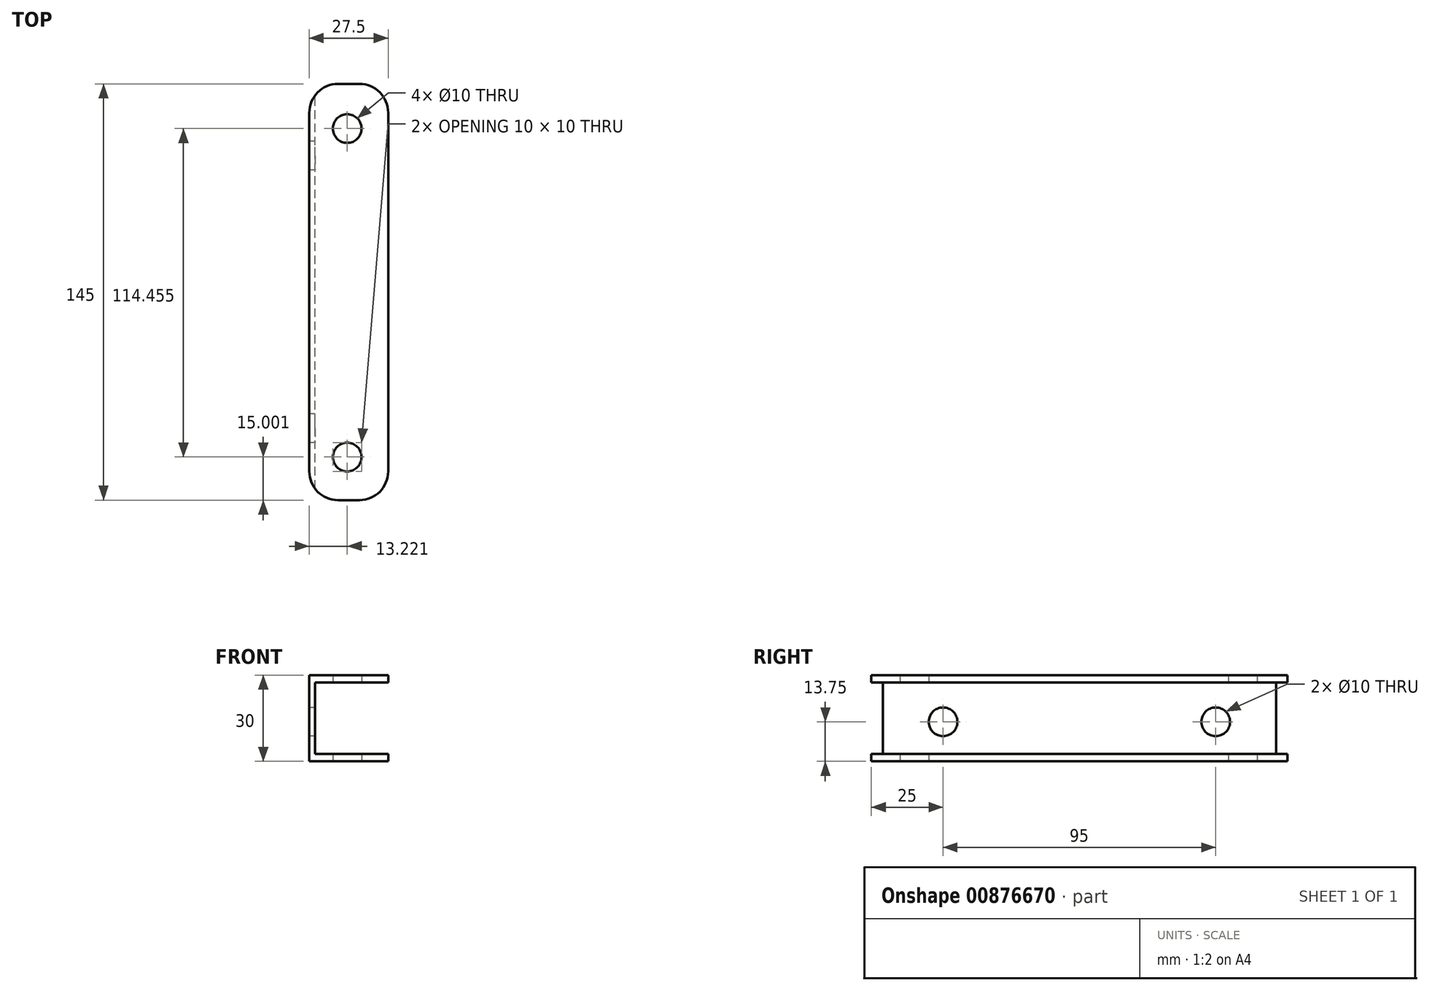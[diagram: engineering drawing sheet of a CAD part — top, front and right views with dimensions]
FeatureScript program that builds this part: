
annotation { "Feature Type Name" : "Feature", "Feature Type Description" : "" }
export const myFeature = defineFeature(function(context is Context, id is Id, definition is map)
    precondition{}
    {
        {
            var Q0;
            Q0=qCreatedBy(makeId("Front.planeOp"),FACE);
            var sketch = newSketch(context, id + "F0", { "sketchPlane" : qUnion([Q0])});
            skLineSegment(sketch, "E0.bottom", {"start": v(-74.99, 0) * mm, "end": v(-47.49, 0) * mm});
            skLineSegment(sketch, "E0.top", {"start": v(-74.99, 30) * mm, "end": v(-47.49, 30) * mm});
            skLineSegment(sketch, "E0.left", {"start": v(-74.99, 0) * mm, "end": v(-74.99, 30) * mm});
            skLineSegment(sketch, "E0.right", {"start": v(-47.49, 0) * mm, "end": v(-47.49, 2.5) * mm});
            skLineSegment(sketch, "E1.top", {"start": v(-47.49, 2.5) * mm, "end": v(-72.99, 2.5) * mm});
            skLineSegment(sketch, "E2.top", {"start": v(-47.49, 27.5) * mm, "end": v(-72.99, 27.5) * mm});
            skLineSegment(sketch, "E3.trimOffspring", {"start": v(-47.49, 27.5) * mm, "end": v(-47.49, 30) * mm});
            skPoint(sketch, "E2.left.start.orphan", {"position": v(-47.49, 15) * mm});
            skLineSegment(sketch, "E4", {"start": v(-72.99, 27.5) * mm, "end": v(-72.99, 2.5) * mm});
            skSolve(sketch);
        }
        {
            var Q0;
            Q0=qCreatedBy(makeId("Top.planeOp"),FACE);
            var sketch = newSketch(context, id + "F1", { "sketchPlane" : qUnion([Q0])});
            skLineSegment(sketch, "E5.bottom", {"start": v(-59.99, -290) * mm, "end": v(-54.99, -290) * mm});
            skCircle(sketch, "E6", {"center": v(-61.77, -15.54) * mm, "radius": 5 * mm});
            skCircle(sketch, "E7", {"center": v(-54.99, -290) * mm, "radius": 5 * mm});
            skCircle(sketch, "E8", {"center": v(-54.99, -260) * mm, "radius": 5 * mm});
            skCircle(sketch, "E9", {"center": v(-61.77, -130) * mm, "radius": 5 * mm});
            skLineSegment(sketch, "E10", {"start": v(-61.77, -15.54) * mm, "end": v(-61.77, -83.7) * mm});
            skSolve(sketch);
        }
        {
            var Q0;
            Q0=makeQuery(id+"F0.imprint","IMPRINT",FACE,{"disambiguationData":[TD([[makeQuery(id+"F0.imprint","IMPRINT",EDGE,{"derivedFrom":sQuery(id+"F0.wireOp",EDGE,"E0.bottom")}),1.0]])]});
            extrude(context, id + "F2", {"entities" : qUnion([Q0]), "depth" : 145 * mm, "offsetDistance" : 25 * mm});
        }
        {
            var Q0;
            Q0=makeQuery(id+"F1.imprint","IMPRINT",FACE,{"disambiguationData":[TD([[makeQuery(id+"F1.imprint","IMPRINT",EDGE,{"derivedFrom":sQuery(id+"F1.wireOp",EDGE,"E7")}),1.0]])]});
            var Q1;
            Q1=makeQuery(id+"F1.imprint","IMPRINT",FACE,{"disambiguationData":[TD([[makeQuery(id+"F1.imprint","IMPRINT",EDGE,{"derivedFrom":sQuery(id+"F1.wireOp",EDGE,"E8")}),1.0]])]});
            var Q2;
            Q2=makeQuery(id+"F1.imprint","IMPRINT",FACE,{"disambiguationData":[TD([[makeQuery(id+"F1.imprint","IMPRINT",EDGE,{"derivedFrom":sQuery(id+"F1.wireOp",EDGE,"E9")}),1.0]])]});
            var Q3;
            Q3=makeQuery(id+"F1.imprint","IMPRINT",FACE,{"disambiguationData":[TD([[makeQuery(id+"F1.imprint","IMPRINT",EDGE,{"derivedFrom":sQuery(id+"F1.wireOp",EDGE,"E6")}),1.0]])]});
            extrude(context, id + "F3", {"entities" : qUnion([Q0, Q1, Q2, Q3]), "operationType" : NewBodyOperationType.REMOVE, "depth" : 46 * mm, "offsetDistance" : 25 * mm});
        }
        {
            var Q0;
            Q0=makeQuery(id+"F2.opExtrude","CAP_EDGE",EDGE,{"disambiguationData":[OSD([sQuery(id+"F0.wireOp",EDGE,"E0.right")])],"isStart":true});
            var Q1;
            Q1=makeQuery(id+"F2.opExtrude","CAP_EDGE",EDGE,{"disambiguationData":[OSD([sQuery(id+"F0.wireOp",EDGE,"E3.trimOffspring")])],"isStart":true});
            var Q2;
            Q2=makeQuery(id+"F2.opExtrude","CAP_EDGE",EDGE,{"disambiguationData":[OSD([sQuery(id+"F0.wireOp",EDGE,"E3.trimOffspring")])],"isStart":false});
            var Q3;
            Q3=makeQuery(id+"F2.opExtrude","CAP_EDGE",EDGE,{"disambiguationData":[OSD([sQuery(id+"F0.wireOp",EDGE,"E0.right")])],"isStart":false});
            var Q4;
            Q4=makeQuery(id+"F2.opExtrude","CAP_EDGE",EDGE,{"disambiguationData":[OSD([sQuery(id+"F0.wireOp",EDGE,"E0.left")])],"isStart":true});
            var Q5;
            Q5=makeQuery(id+"F2.opExtrude","CAP_EDGE",EDGE,{"disambiguationData":[OSD([sQuery(id+"F0.wireOp",EDGE,"E0.left")])],"isStart":false});
            fillet(context, id + "F4", {"entities" : qUnion([Q0, Q1, Q2, Q3, Q4, Q5]), "radius" : 10 * mm, "tangentPropagation" : true, "allowEdgeOverflow" : false});
        }
        {
            var Q0;
            Q0=makeQuery(id+"F2.opExtrude","SWEPT_FACE",FACE,{"disambiguationData":[OSD([sQuery(id+"F0.wireOp",EDGE,"E0.left")])]});
            cPlane(context, id + "F5", {"entities" : qUnion([Q0]), "cplaneType" : CPlaneType.OFFSET, "offset" : 0 * mm, "width" : 150 * mm, "height" : 150 * mm});
        }
        {
            var Q0;
            Q0=qCreatedBy(id+"F5.planeOp",FACE);
            var sketch = newSketch(context, id + "F6", { "sketchPlane" : qUnion([Q0])});
            skLineSegment(sketch, "E11.bottom", {"start": v(10, 30) * mm, "end": v(130, 30) * mm});
            skLineSegment(sketch, "E11.top", {"start": v(10, 0) * mm, "end": v(130, 0) * mm});
            skLineSegment(sketch, "E11.left", {"start": v(10, 30) * mm, "end": v(10, 0) * mm});
            skLineSegment(sketch, "E11.right", {"start": v(130, 30) * mm, "end": v(130, 0) * mm});
            skLineSegment(sketch, "E12.bottom", {"start": v(130, 0) * mm, "end": v(25, 0) * mm});
            skLineSegment(sketch, "E12.top", {"start": v(130, 13.75) * mm, "end": v(25, 13.75) * mm});
            skLineSegment(sketch, "E12.left", {"start": v(130, 0) * mm, "end": v(130, 13.75) * mm});
            skLineSegment(sketch, "E12.right", {"start": v(25, 0) * mm, "end": v(25, 13.75) * mm});
            skLineSegment(sketch, "E13", {"start": v(120, 13.75) * mm, "end": v(130, 13.75) * mm});
            skCircle(sketch, "E14", {"center": v(25, 13.75) * mm, "radius": 5 * mm});
            skCircle(sketch, "E15", {"center": v(120, 13.75) * mm, "radius": 5 * mm});
            skSolve(sketch);
        }
        {
            var Q0;
            {var subQ0=sQuery(id+"F6.wireOp",EDGE,"E12.right");var subQ1=sQuery(id+"F6.wireOp",EDGE,"E12.top");var subQ2=makeQuery(id+"F6.imprint","INTERSECT",VERTEX,{"derivedFrom":[subQ1,subQ0]});Q0=makeQuery(id+"F6.imprint","IMPRINT",FACE,{"disambiguationData":[TD([[makeQuery(id+"F6.imprint","IMPRINT",EDGE,{"disambiguationData":[TD([[subQ2,1.0]])],"derivedFrom":subQ1}),-1.0]])]});}
            var Q1;
            {var subQ0=sQuery(id+"F6.wireOp",EDGE,"E12.right");var subQ1=sQuery(id+"F6.wireOp",EDGE,"E12.top");var subQ2=makeQuery(id+"F6.imprint","INTERSECT",VERTEX,{"derivedFrom":[subQ1,subQ0]});Q1=makeQuery(id+"F6.imprint","IMPRINT",FACE,{"disambiguationData":[TD([[makeQuery(id+"F6.imprint","IMPRINT",EDGE,{"disambiguationData":[TD([[subQ2,1.0]])],"derivedFrom":subQ1}),1.0]])]});}
            var Q2;
            Q2=makeQuery(id+"F6.imprint","IMPRINT",FACE,{"disambiguationData":[TD([[makeQuery(id+"F6.imprint","IMPRINT",EDGE,{"derivedFrom":sQuery(id+"F6.wireOp",EDGE,"E15")}),1.0]])]});
            extrude(context, id + "F7", {"entities" : qUnion([Q0, Q1, Q2]), "operationType" : NewBodyOperationType.REMOVE, "oppositeDirection" : true, "depth" : 25 * mm, "offsetDistance" : 25 * mm});
        }
    });
